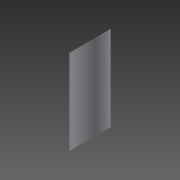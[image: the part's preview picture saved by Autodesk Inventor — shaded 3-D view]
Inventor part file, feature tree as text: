
AUTODESK INVENTOR PART (.ipt)
format: ipt  version: 2015 (Build 190159000, 159)  size: 93,184 bytes
history: native  units: mm
features: other x3, extrude x1, shell x1, sketch x1
ambient origin geometry x8: Origin, YZ Plane, XZ Plane, XY Plane, X Axis, Y Axis, Z Axis, Center Point
bodies: Body1 (feature_tree)
feature tree (6):
  other  "Bryła1"
  extrude  "Wyciągnięcie proste1"  Depth=32.0mm
  shell  "Skorupa1"  Thickness=150.0mm
  other  "Podział1"
  other  "Podział2"
  sketch  "Szkic1"
